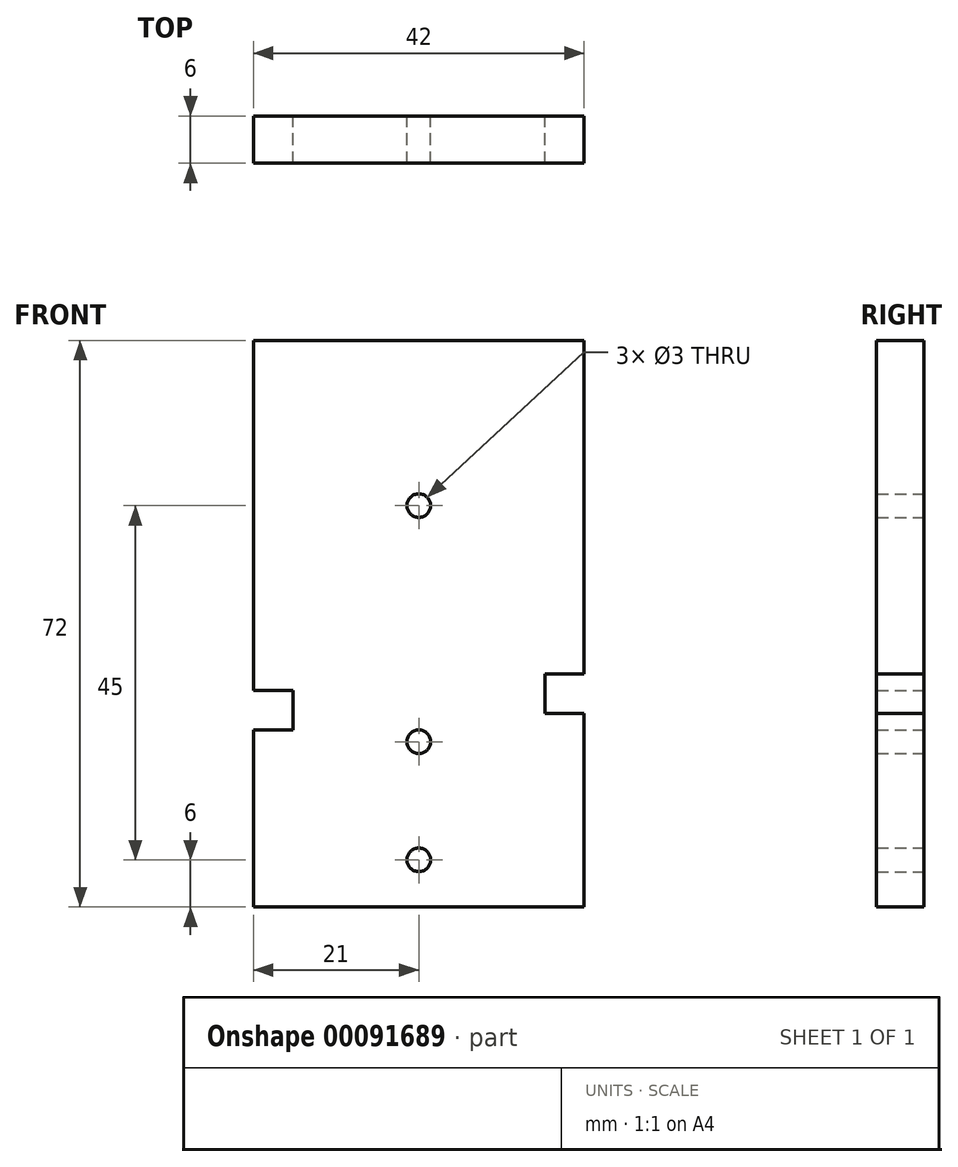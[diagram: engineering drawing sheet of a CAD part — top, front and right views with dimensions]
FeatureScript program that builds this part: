
annotation { "Feature Type Name" : "Feature", "Feature Type Description" : "" }
export const myFeature = defineFeature(function(context is Context, id is Id, definition is map)
    precondition{}
    {
        {
            var Q0;
            Q0=qCreatedBy(makeId("Front.planeOp"),FACE);
            var sketch = newSketch(context, id + "F0", { "sketchPlane" : qUnion([Q0])});
            skLineSegment(sketch, "E0.bottom", {"start": v(0, 0) * mm, "end": v(42, 0) * mm});
            skLineSegment(sketch, "E0.top", {"start": v(0, 72) * mm, "end": v(42, 72) * mm});
            skLineSegment(sketch, "E0.left", {"start": v(0, 0) * mm, "end": v(0, 72) * mm});
            skLineSegment(sketch, "E0.right", {"start": v(42, 0) * mm, "end": v(42, 72) * mm});
            skLineSegment(sketch, "E1.bottom", {"start": v(0, 22.5) * mm, "end": v(5, 22.5) * mm});
            skLineSegment(sketch, "E1.top", {"start": v(0, 27.5) * mm, "end": v(5, 27.5) * mm});
            skLineSegment(sketch, "E1.left", {"start": v(0, 22.5) * mm, "end": v(0, 27.5) * mm});
            skLineSegment(sketch, "E1.right", {"start": v(5, 22.5) * mm, "end": v(5, 27.5) * mm});
            skLineSegment(sketch, "E2.bottom", {"start": v(42, 29.58) * mm, "end": v(37, 29.58) * mm});
            skLineSegment(sketch, "E2.top", {"start": v(42, 24.58) * mm, "end": v(37, 24.58) * mm});
            skLineSegment(sketch, "E2.left", {"start": v(42, 29.58) * mm, "end": v(42, 24.58) * mm});
            skLineSegment(sketch, "E2.right", {"start": v(37, 29.58) * mm, "end": v(37, 24.58) * mm});
            skLineSegment(sketch, "E3.bottom", {"start": v(-111.04, 229.24) * mm, "end": v(104.86, 229.24) * mm});
            skLineSegment(sketch, "E3.top", {"start": v(-111.04, -50.16) * mm, "end": v(104.86, -50.16) * mm});
            skLineSegment(sketch, "E3.left", {"start": v(-111.04, 229.24) * mm, "end": v(-111.04, -50.16) * mm});
            skLineSegment(sketch, "E3.right", {"start": v(104.86, 229.24) * mm, "end": v(104.86, -50.16) * mm});
            skLineSegment(sketch, "E4", {"start": v(0, 72) * mm, "end": v(0, 51) * mm});
            skLineSegment(sketch, "E5", {"start": v(0, 51) * mm, "end": v(21, 51) * mm});
            skCircle(sketch, "E6", {"center": v(21, 51) * mm, "radius": 1.5 * mm});
            skLineSegment(sketch, "E7", {"start": v(0, 72) * mm, "end": v(0, 33.33) * mm});
            skLineSegment(sketch, "E8", {"start": v(21, 51) * mm, "end": v(21, 21) * mm});
            skCircle(sketch, "E9", {"center": v(21, 21) * mm, "radius": 1.5 * mm});
            skLineSegment(sketch, "E10", {"start": v(21, 21) * mm, "end": v(21, 6) * mm});
            skCircle(sketch, "E11", {"center": v(21, 6) * mm, "radius": 1.5 * mm});
            skSolve(sketch);
        }
        {
            var Q0;
            {var subQ1=sQuery(id+"F0.wireOp",EDGE,"E0.bottom");Q0=makeQuery(id+"F0.imprint","IMPRINT",FACE,{"disambiguationData":[TD([[makeQuery(id+"F0.imprint","IMPRINT",EDGE,{"derivedFrom":subQ1}),1.0]])]});}
            extrude(context, id + "F1", {"entities" : qUnion([Q0]), "depth" : 6 * mm});
        }
    });
